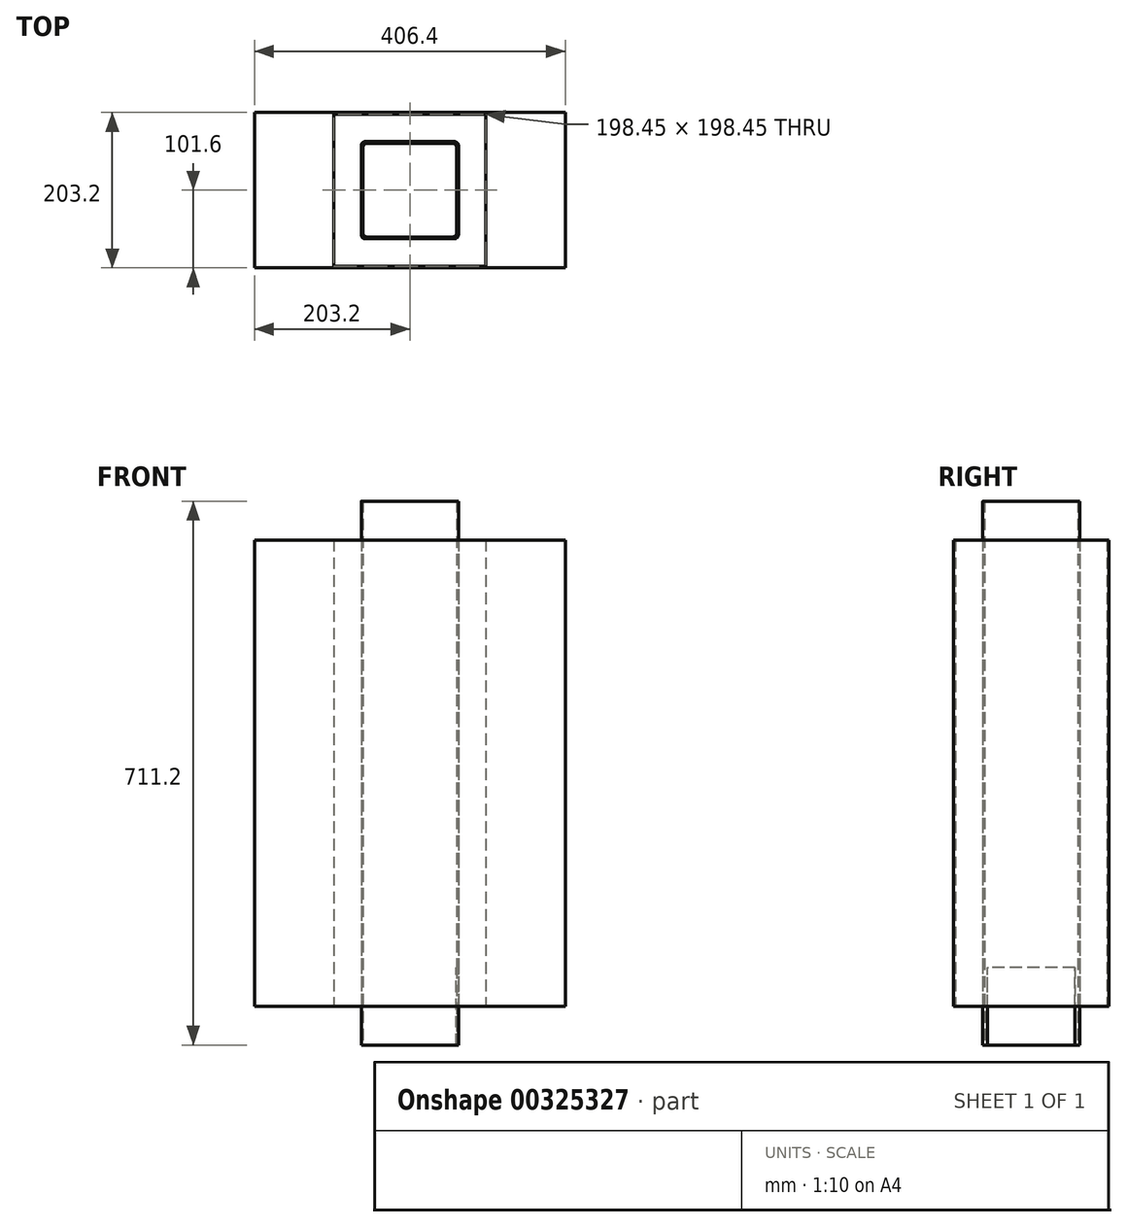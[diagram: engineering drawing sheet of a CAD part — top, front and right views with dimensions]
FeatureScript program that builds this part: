
annotation { "Feature Type Name" : "Feature", "Feature Type Description" : "" }
export const myFeature = defineFeature(function(context is Context, id is Id, definition is map)
    precondition{}
    {
        {
            var Q0;
            Q0=qCreatedBy(makeId("Top.planeOp"),FACE);
            var sketch = newSketch(context, id + "F0", { "sketchPlane" : qUnion([Q0])});
            skLineSegment(sketch, "E0.bottom", {"start": v(-63.5, 63.5) * mm, "end": v(63.5, 63.5) * mm});
            skLineSegment(sketch, "E0.top", {"start": v(-63.5, -63.5) * mm, "end": v(63.5, -63.5) * mm});
            skLineSegment(sketch, "E0.left", {"start": v(-63.5, 63.5) * mm, "end": v(-63.5, -63.5) * mm});
            skLineSegment(sketch, "E0.right", {"start": v(63.5, 63.5) * mm, "end": v(63.5, -63.5) * mm});
            skPoint(sketch, "E0.middle", {"position": v(0, 0) * mm});
            skLineSegment(sketch, "E1.bottom", {"start": v(61.12, 61.12) * mm, "end": v(-61.12, 61.12) * mm});
            skLineSegment(sketch, "E1.top", {"start": v(61.12, -61.12) * mm, "end": v(-61.12, -61.12) * mm});
            skLineSegment(sketch, "E1.left", {"start": v(61.12, 61.12) * mm, "end": v(61.12, -61.12) * mm});
            skLineSegment(sketch, "E1.right", {"start": v(-61.12, 61.12) * mm, "end": v(-61.12, -61.12) * mm});
            skLineSegment(sketch, "E2.bottom", {"start": v(203.2, -101.6) * mm, "end": v(-203.2, -101.6) * mm});
            skLineSegment(sketch, "E2.top", {"start": v(203.2, 101.6) * mm, "end": v(-203.2, 101.6) * mm});
            skLineSegment(sketch, "E2.left", {"start": v(203.2, -101.6) * mm, "end": v(203.2, 101.6) * mm});
            skLineSegment(sketch, "E2.right", {"start": v(-203.2, -101.6) * mm, "end": v(-203.2, 101.6) * mm});
            skLineSegment(sketch, "E3.bottom", {"start": v(99.23, -99.23) * mm, "end": v(-99.23, -99.23) * mm});
            skLineSegment(sketch, "E3.top", {"start": v(99.23, 99.23) * mm, "end": v(-99.23, 99.23) * mm});
            skLineSegment(sketch, "E3.left", {"start": v(99.23, -99.23) * mm, "end": v(99.23, 99.23) * mm});
            skLineSegment(sketch, "E3.right", {"start": v(-99.23, -99.23) * mm, "end": v(-99.23, 99.23) * mm});
            skSolve(sketch);
        }
        {
            var Q0;
            Q0=makeQuery(id+"F0.imprint","IMPRINT",FACE,{"disambiguationData":[TD([[makeQuery(id+"F0.imprint","IMPRINT",EDGE,{"derivedFrom":sQuery(id+"F0.wireOp",EDGE,"E0.bottom")}),-1.0]])]});
            extrude(context, id + "F1", {"entities" : qUnion([Q0]), "depth" : 711.2 * mm});
        }
        {
            var Q0;
            Q0=makeQuery(id+"F1.opExtrude","SWEPT_EDGE",EDGE,{"disambiguationData":[OSD([sQuery(id+"F0.wireOp",EDGE,"E0.bottom"),sQuery(id+"F0.wireOp",EDGE,"E0.right")])]});
            var Q1;
            Q1=makeQuery(id+"F1.opExtrude","SWEPT_EDGE",EDGE,{"disambiguationData":[OSD([sQuery(id+"F0.wireOp",EDGE,"E0.bottom"),sQuery(id+"F0.wireOp",EDGE,"E0.left")])]});
            var Q2;
            Q2=makeQuery(id+"F1.opExtrude","SWEPT_EDGE",EDGE,{"disambiguationData":[OSD([sQuery(id+"F0.wireOp",EDGE,"E0.top"),sQuery(id+"F0.wireOp",EDGE,"E0.left")])]});
            var Q3;
            Q3=makeQuery(id+"F1.opExtrude","SWEPT_EDGE",EDGE,{"disambiguationData":[OSD([sQuery(id+"F0.wireOp",EDGE,"E0.top"),sQuery(id+"F0.wireOp",EDGE,"E0.right")])]});
            var Q4;
            Q4=makeQuery(id+"F1.opExtrude","SWEPT_EDGE",EDGE,{"disambiguationData":[OSD([sQuery(id+"F0.wireOp",EDGE,"E1.bottom"),sQuery(id+"F0.wireOp",EDGE,"E1.right")])]});
            var Q5;
            Q5=makeQuery(id+"F1.opExtrude","SWEPT_EDGE",EDGE,{"disambiguationData":[OSD([sQuery(id+"F0.wireOp",EDGE,"E1.top"),sQuery(id+"F0.wireOp",EDGE,"E1.right")])]});
            var Q6;
            Q6=makeQuery(id+"F1.opExtrude","SWEPT_EDGE",EDGE,{"disambiguationData":[OSD([sQuery(id+"F0.wireOp",EDGE,"E1.top"),sQuery(id+"F0.wireOp",EDGE,"E1.left")])]});
            var Q7;
            Q7=makeQuery(id+"F1.opExtrude","SWEPT_EDGE",EDGE,{"disambiguationData":[OSD([sQuery(id+"F0.wireOp",EDGE,"E1.bottom"),sQuery(id+"F0.wireOp",EDGE,"E1.left")])]});
            fillet(context, id + "F2", {"entities" : qUnion([Q0, Q1, Q2, Q3, Q4, Q5, Q6, Q7]), "radius" : 5.08 * mm, "tangentPropagation" : true, "allowEdgeOverflow" : false});
        }
        {
            var Q0;
            Q0=makeQuery(id+"F1.opExtrude","SWEPT_BODY",BODY,{"disambiguationData":[OSD([sQuery(id+"F0.wireOp",EDGE,"E0.bottom"),sQuery(id+"F0.wireOp",EDGE,"E0.top"),sQuery(id+"F0.wireOp",EDGE,"E0.left"),sQuery(id+"F0.wireOp",EDGE,"E0.right"),sQuery(id+"F0.wireOp",EDGE,"E1.bottom"),sQuery(id+"F0.wireOp",EDGE,"E1.top"),sQuery(id+"F0.wireOp",EDGE,"E1.left"),sQuery(id+"F0.wireOp",EDGE,"E1.right")])]});
            transform(context, id + "F3", {"entities" : qUnion([Q0]), "transformType" : TransformType.TRANSLATION_3D, "dx" : 0 * mm, "dy" : 0 * mm, "dz" : -50.8 * mm, "makeCopy" : false});
        }
        {
            var Q0;
            Q0=qCreatedBy(makeId("Right.planeOp"),FACE);
            var sketch = newSketch(context, id + "F4", { "sketchPlane" : qUnion([Q0])});
            skLineSegment(sketch, "E4.bottom", {"start": v(49.46, -101.6) * mm, "end": v(-64.84, -101.6) * mm});
            skPoint(sketch, "E4.middle", {"position": v(0, 0) * mm});
            skLineSegment(sketch, "E5", {"start": v(-64.84, 0) * mm, "end": v(49.46, 0) * mm});
            skLineSegment(sketch, "E6", {"start": v(-64.84, 0) * mm, "end": v(-64.84, -101.6) * mm});
            skLineSegment(sketch, "E7", {"start": v(49.46, 0) * mm, "end": v(49.46, -101.6) * mm});
            skSolve(sketch);
        }
        {
            var Q0;
            Q0 = qSketchRegion(id + "F0", true);
            extrude(context, id + "F5", {"entities" : qUnion([Q0]), "depth" : 609.6 * mm});
        }
        {
            var Q0;
            Q0=makeQuery(id+"F0.imprint","IMPRINT",FACE,{"disambiguationData":[TD([[makeQuery(id+"F0.imprint","IMPRINT",EDGE,{"derivedFrom":sQuery(id+"F0.wireOp",EDGE,"E0.bottom")}),-1.0]])]});
            extrude(context, id + "F6", {"entities" : qUnion([Q0]), "depth" : 457.2 * mm});
        }
        {
            var Q0;
            Q0=makeQuery(id+"F6.opExtrude","SWEPT_EDGE",EDGE,{"disambiguationData":[OSD([sQuery(id+"F0.wireOp",EDGE,"E0.top"),sQuery(id+"F0.wireOp",EDGE,"E0.left")])]});
            var Q1;
            Q1=makeQuery(id+"F6.opExtrude","SWEPT_EDGE",EDGE,{"disambiguationData":[OSD([sQuery(id+"F0.wireOp",EDGE,"E0.bottom"),sQuery(id+"F0.wireOp",EDGE,"E0.left")])]});
            var Q2;
            Q2=makeQuery(id+"F6.opExtrude","SWEPT_EDGE",EDGE,{"disambiguationData":[OSD([sQuery(id+"F0.wireOp",EDGE,"E0.top"),sQuery(id+"F0.wireOp",EDGE,"E0.right")])]});
            var Q3;
            Q3=makeQuery(id+"F6.opExtrude","SWEPT_EDGE",EDGE,{"disambiguationData":[OSD([sQuery(id+"F0.wireOp",EDGE,"E0.bottom"),sQuery(id+"F0.wireOp",EDGE,"E0.right")])]});
            var Q4;
            Q4=makeQuery(id+"F6.opExtrude","SWEPT_EDGE",EDGE,{"disambiguationData":[OSD([sQuery(id+"F0.wireOp",EDGE,"E1.top"),sQuery(id+"F0.wireOp",EDGE,"E1.right")])]});
            var Q5;
            Q5=makeQuery(id+"F6.opExtrude","SWEPT_EDGE",EDGE,{"disambiguationData":[OSD([sQuery(id+"F0.wireOp",EDGE,"E1.bottom"),sQuery(id+"F0.wireOp",EDGE,"E1.right")])]});
            var Q6;
            Q6=makeQuery(id+"F6.opExtrude","SWEPT_EDGE",EDGE,{"disambiguationData":[OSD([sQuery(id+"F0.wireOp",EDGE,"E1.bottom"),sQuery(id+"F0.wireOp",EDGE,"E1.left")])]});
            var Q7;
            Q7=makeQuery(id+"F6.opExtrude","SWEPT_EDGE",EDGE,{"disambiguationData":[OSD([sQuery(id+"F0.wireOp",EDGE,"E1.top"),sQuery(id+"F0.wireOp",EDGE,"E1.left")])]});
            fillet(context, id + "F7", {"entities" : qUnion([Q0, Q1, Q2, Q3, Q4, Q5, Q6, Q7]), "radius" : 5.08 * mm, "tangentPropagation" : true, "allowEdgeOverflow" : false});
        }
        {
            var Q0;
            Q0=makeQuery(id+"F6.opExtrude","SWEPT_BODY",BODY,{"disambiguationData":[OSD([sQuery(id+"F0.wireOp",EDGE,"E0.bottom"),sQuery(id+"F0.wireOp",EDGE,"E0.top"),sQuery(id+"F0.wireOp",EDGE,"E0.left"),sQuery(id+"F0.wireOp",EDGE,"E0.right"),sQuery(id+"F0.wireOp",EDGE,"E1.bottom"),sQuery(id+"F0.wireOp",EDGE,"E1.top"),sQuery(id+"F0.wireOp",EDGE,"E1.left"),sQuery(id+"F0.wireOp",EDGE,"E1.right")])]});
            transform(context, id + "F8", {"entities" : qUnion([Q0]), "transformType" : TransformType.TRANSLATION_3D, "dx" : 0 * mm, "dy" : 0 * mm, "dz" : 101.6 * mm, "makeCopy" : false});
        }
        {
            var Q0;
            Q0=makeQuery(id+"F6.opExtrude","SWEPT_BODY",BODY,{"disambiguationData":[OSD([sQuery(id+"F0.wireOp",EDGE,"E0.bottom"),sQuery(id+"F0.wireOp",EDGE,"E0.top"),sQuery(id+"F0.wireOp",EDGE,"E0.left"),sQuery(id+"F0.wireOp",EDGE,"E0.right"),sQuery(id+"F0.wireOp",EDGE,"E1.bottom"),sQuery(id+"F0.wireOp",EDGE,"E1.top"),sQuery(id+"F0.wireOp",EDGE,"E1.left"),sQuery(id+"F0.wireOp",EDGE,"E1.right")])]});
            var Q1;
            Q1=makeQuery(id+"F6.opExtrude","CAP_EDGE",EDGE,{"disambiguationData":[OSD([sQuery(id+"F0.wireOp",EDGE,"E0.right")])],"isStart":true});
            transform(context, id + "F9", {"entities" : qUnion([Q0]), "transformType" : TransformType.ROTATION, "transformAxis" : qUnion([Q1]), "angle" : 35 * degree, "oppositeDirection" : true, "makeCopy" : false});
        }
        {
            var Q0;
            Q0=makeQuery(id+"F1.opExtrude","SWEPT_BODY",BODY,{"disambiguationData":[OSD([sQuery(id+"F0.wireOp",EDGE,"E0.bottom"),sQuery(id+"F0.wireOp",EDGE,"E0.top"),sQuery(id+"F0.wireOp",EDGE,"E0.left"),sQuery(id+"F0.wireOp",EDGE,"E0.right"),sQuery(id+"F0.wireOp",EDGE,"E1.bottom"),sQuery(id+"F0.wireOp",EDGE,"E1.top"),sQuery(id+"F0.wireOp",EDGE,"E1.left"),sQuery(id+"F0.wireOp",EDGE,"E1.right")])]});
            var Q1;
            Q1=makeQuery(id+"F6.opExtrude","SWEPT_BODY",BODY,{"disambiguationData":[OSD([sQuery(id+"F0.wireOp",EDGE,"E0.bottom"),sQuery(id+"F0.wireOp",EDGE,"E0.top"),sQuery(id+"F0.wireOp",EDGE,"E0.left"),sQuery(id+"F0.wireOp",EDGE,"E0.right"),sQuery(id+"F0.wireOp",EDGE,"E1.bottom"),sQuery(id+"F0.wireOp",EDGE,"E1.top"),sQuery(id+"F0.wireOp",EDGE,"E1.left"),sQuery(id+"F0.wireOp",EDGE,"E1.right")])]});
            booleanBodies(context, id + "F10", {"operationType" : BooleanOperationType.SUBTRACTION, "tools" : qUnion([Q0]), "targets" : qUnion([Q1]), "keepTools" : true});
        }
        {
            var Q0;
            Q0=makeQuery(id+"F10.opBoolean","SPLIT",BODY,{"disambiguationData":[OD(0.0)],"derivedFrom":makeQuery(id+"F6.opExtrude","SWEPT_BODY",BODY,{"disambiguationData":[OSD([sQuery(id+"F0.wireOp",EDGE,"E0.bottom"),sQuery(id+"F0.wireOp",EDGE,"E0.top"),sQuery(id+"F0.wireOp",EDGE,"E0.left"),sQuery(id+"F0.wireOp",EDGE,"E0.right"),sQuery(id+"F0.wireOp",EDGE,"E1.bottom"),sQuery(id+"F0.wireOp",EDGE,"E1.top"),sQuery(id+"F0.wireOp",EDGE,"E1.left"),sQuery(id+"F0.wireOp",EDGE,"E1.right")])]})});
            deleteBodies(context, id + "F11", {"entities" : qUnion([Q0])});
        }
        {
            var Q0;
            Q0=makeQuery(id+"F4.imprint","IMPRINT",FACE,{"disambiguationData":[TD([[makeQuery(id+"F4.imprint","IMPRINT",EDGE,{"derivedFrom":sQuery(id+"F4.wireOp",EDGE,"E4.bottom")}),-1.0]])]});
            extrude(context, id + "F12", {"entities" : qUnion([Q0]), "depth" : 152.4 * mm});
        }
        {
            var Q0;
            Q0=makeQuery(id+"F12.opExtrude","SWEPT_BODY",BODY,{"disambiguationData":[OSD([sQuery(id+"F4.wireOp",EDGE,"E4.bottom"),sQuery(id+"F4.wireOp",EDGE,"E5"),sQuery(id+"F4.wireOp",EDGE,"E6"),sQuery(id+"F4.wireOp",EDGE,"E7")])]});
            transform(context, id + "F13", {"entities" : qUnion([Q0]), "transformType" : TransformType.TRANSLATION_3D, "dx" : 0 * mm, "dy" : 7.37 * mm, "dz" : 50.8 * mm, "makeCopy" : false});
        }
        {
            var Q0;
            Q0=makeQuery(id+"F12.opExtrude","SWEPT_BODY",BODY,{"disambiguationData":[OSD([sQuery(id+"F4.wireOp",EDGE,"E4.bottom"),sQuery(id+"F4.wireOp",EDGE,"E5"),sQuery(id+"F4.wireOp",EDGE,"E6"),sQuery(id+"F4.wireOp",EDGE,"E7")])]});
            var Q1;
            Q1=makeQuery(id+"F1.opExtrude","SWEPT_BODY",BODY,{"disambiguationData":[OSD([sQuery(id+"F0.wireOp",EDGE,"E0.bottom"),sQuery(id+"F0.wireOp",EDGE,"E0.top"),sQuery(id+"F0.wireOp",EDGE,"E0.left"),sQuery(id+"F0.wireOp",EDGE,"E0.right"),sQuery(id+"F0.wireOp",EDGE,"E1.bottom"),sQuery(id+"F0.wireOp",EDGE,"E1.top"),sQuery(id+"F0.wireOp",EDGE,"E1.left"),sQuery(id+"F0.wireOp",EDGE,"E1.right")])]});
            booleanBodies(context, id + "F14", {"operationType" : BooleanOperationType.SUBTRACTION, "tools" : qUnion([Q0]), "targets" : qUnion([Q1])});
        }
    });
